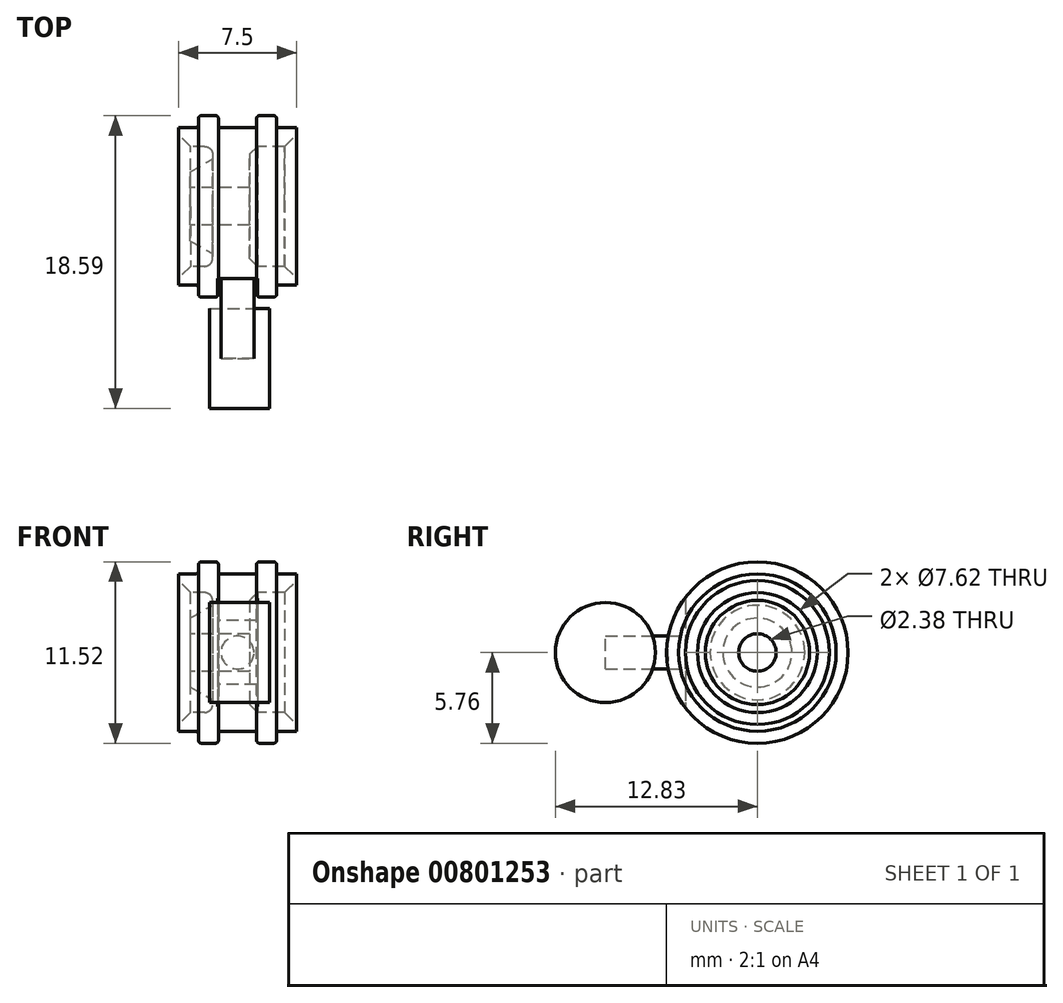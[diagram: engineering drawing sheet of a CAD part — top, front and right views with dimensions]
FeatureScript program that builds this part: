
annotation { "Feature Type Name" : "Feature", "Feature Type Description" : "" }
export const myFeature = defineFeature(function(context is Context, id is Id, definition is map)
    precondition{}
    {
        {
            var Q0;
            Q0=qCreatedBy(makeId("Front.planeOp"),FACE);
            var sketch = newSketch(context, id + "F0", { "sketchPlane" : qUnion([Q0])});
            skLineSegment(sketch, "E0", {"start": v(-3, 1.2) * mm, "end": v(0.76, 1.2) * mm});
            skLineSegment(sketch, "E1", {"start": v(0.76, 1.2) * mm, "end": v(0.76, 3.31) * mm});
            skLineSegment(sketch, "E2", {"start": v(1.26, 3.81) * mm, "end": v(3.75, 3.81) * mm});
            skLineSegment(sketch, "E3", {"start": v(3.75, 3.81) * mm, "end": v(3.75, 5) * mm});
            skLineSegment(sketch, "E4", {"start": v(3.75, 5) * mm, "end": v(2.48, 5) * mm});
            skLineSegment(sketch, "E5", {"start": v(2.48, 5) * mm, "end": v(2.48, 5.76) * mm});
            skLineSegment(sketch, "E6", {"start": v(2.48, 5.76) * mm, "end": v(1.21, 5.76) * mm});
            skLineSegment(sketch, "E7", {"start": v(-2.48, 5.76) * mm, "end": v(-2.48, 5) * mm});
            skLineSegment(sketch, "E8", {"start": v(-2.48, 5) * mm, "end": v(-3.75, 5) * mm});
            skLineSegment(sketch, "E9", {"start": v(-3.75, 5) * mm, "end": v(-3.75, 3.8) * mm});
            skLineSegment(sketch, "E10", {"start": v(-1.59, 3) * mm, "end": v(-3, 2.2) * mm});
            skLineSegment(sketch, "E11", {"start": v(-3, 2.2) * mm, "end": v(-3, 1.2) * mm});
            skLineSegment(sketch, "E12", {"start": v(0, 5.76) * mm, "end": v(0, 0) * mm, "construction": true});
            skLineSegment(sketch, "E13", {"start": v(0, 0) * mm, "end": v(34.63, 0) * mm});
            skLineSegment(sketch, "E14.left", {"start": v(-1.21, 5.76) * mm, "end": v(-1.21, 5) * mm});
            skLineSegment(sketch, "E14.right", {"start": v(1.21, 5.76) * mm, "end": v(1.21, 5) * mm});
            skLineSegment(sketch, "E15.trimOffspring", {"start": v(-1.21, 5.76) * mm, "end": v(-2.48, 5.76) * mm});
            skLineSegment(sketch, "E16", {"start": v(-1.59, 3) * mm, "end": v(-1.59, 3.31) * mm});
            skArc(sketch, "E17.filletArc", {"start": v(-1.59, 3.31) * mm, "mid": v(-1.73, 3.66) * mm, "end": v(-2.09, 3.81) * mm});
            skLineSegment(sketch, "E18", {"start": v(0.76, 3.31) * mm, "end": v(1.26, 3.81) * mm});
            skLineSegment(sketch, "E19", {"start": v(-1.21, 5) * mm, "end": v(1.21, 5) * mm});
            skLineSegment(sketch, "E20", {"start": v(-3.75, 4.4) * mm, "end": v(0, 4.4) * mm, "construction": true});
            skLineSegment(sketch, "E21", {"start": v(0, 4.4) * mm, "end": v(3.75, 4.4) * mm, "construction": true});
            skLineSegment(sketch, "E22", {"start": v(-1.21, 5.76) * mm, "end": v(0, 5.76) * mm, "construction": true});
            skLineSegment(sketch, "E23", {"start": v(0, 5.76) * mm, "end": v(1.21, 5.76) * mm, "construction": true});
            skLineSegment(sketch, "E24", {"start": v(-3.75, 3.81) * mm, "end": v(-2.09, 3.81) * mm});
            skSolve(sketch);
        }
        {
            var Q0;
            Q0=qSketchRegion(id+"F0",true);
            var Q1;
            Q1=sQuery(id+"F0.wireOp",EDGE,"E13");
            revolve(context, id + "F1", {"surfaceOperationType" : NewSurfaceOperationType.NEW, "entities" : qUnion([Q0]), "axis" : qUnion([Q1]), "revolveType" : RevolveType.FULL});
        }
        {
            var Q0;
            Q0=makeQuery(id+"F1.opRevolve","SWEPT_EDGE",EDGE,{"disambiguationData":[OSD([sQuery(id+"F0.wireOp",EDGE,"E5"),sQuery(id+"F0.wireOp",EDGE,"E6")])]});
            var Q1;
            Q1=makeQuery(id+"F1.opRevolve","SWEPT_EDGE",EDGE,{"disambiguationData":[OSD([sQuery(id+"F0.wireOp",EDGE,"E6"),sQuery(id+"F0.wireOp",EDGE,"E7")])]});
            var Q2;
            Q2=makeQuery(id+"F1.opRevolve","SWEPT_EDGE",EDGE,{"disambiguationData":[OSD([sQuery(id+"F0.wireOp",EDGE,"E14.left"),sQuery(id+"F0.wireOp",EDGE,"E15.trimOffspring")])]});
            fillet(context, id + "F2", {"entities" : qUnion([Q0, Q1, Q2]), "radius" : 0.2 * mm, "tangentPropagation" : true, "allowEdgeOverflow" : false});
        }
        {
            var Q0;
            Q0=makeQuery(id+"F1.opRevolve","SWEPT_EDGE",EDGE,{"disambiguationData":[OSD([sQuery(id+"F0.wireOp",EDGE,"E2"),sQuery(id+"F0.wireOp",EDGE,"E3")])]});
            var Q1;
            Q1=makeQuery(id+"F1.opRevolve","SWEPT_EDGE",EDGE,{"disambiguationData":[OSD([sQuery(id+"F0.wireOp",EDGE,"E9"),sQuery(id+"F0.wireOp",EDGE,"E24")])]});
            chamfer(context, id + "F3", {"entities" : qUnion([Q0, Q1]), "width" : 0.76 * mm, "tangentPropagation" : true});
        }
        {
            var Q0;
            Q0=qCreatedBy(makeId("Right.planeOp"),FACE);
            var sketch = newSketch(context, id + "F4", { "sketchPlane" : qUnion([Q0])});
            skLineSegment(sketch, "E25.bottom", {"start": v(-8.57, 4.73) * mm, "end": v(-4.57, 4.73) * mm});
            skLineSegment(sketch, "E25.top", {"start": v(-8.57, -4.76) * mm, "end": v(-4.57, -4.76) * mm});
            skLineSegment(sketch, "E25.left", {"start": v(-8.57, 4.73) * mm, "end": v(-8.57, -4.76) * mm});
            skLineSegment(sketch, "E25.right", {"start": v(-4.57, 4.73) * mm, "end": v(-4.57, -4.76) * mm});
            skSolve(sketch);
        }
        {
            var Q0;
            Q0=qSketchRegion(id+"F4",true);
            extrude(context, id + "F5", {"entities" : qUnion([Q0]), "operationType" : NewBodyOperationType.REMOVE, "oppositeDirection" : true, "depth" : 2.54 * mm, "offsetDistance" : 25.4 * mm, "symmetric" : true});
        }
        {
            var Q0;
            Q0=makeQuery(id+"F5.boolean.opBoolean","COPY",FACE,{"derivedFrom":makeQuery(id+"F5.opExtrude","SWEPT_FACE",FACE,{"disambiguationData":[OSD([sQuery(id+"F4.wireOp",EDGE,"E25.right")])]})});
            var sketch = newSketch(context, id + "F6", { "sketchPlane" : qUnion([Q0])});
            skCircle(sketch, "E26", {"center": v(0, 0) * mm, "radius": 1.05 * mm});
            skSolve(sketch);
        }
        {
            var Q0;
            Q0=qSketchRegion(id+"F6",true);
            extrude(context, id + "F7", {"entities" : qUnion([Q0]), "operationType" : NewBodyOperationType.ADD, "depth" : 5.08 * mm, "offsetDistance" : 25.4 * mm, "hasSecondDirection" : true, "secondDirectionBound" : BoundingType.UP_TO_NEXT, "secondDirectionOppositeDirection" : true, "secondDirectionDepth" : 25.4 * mm});
        }
        {
            var Q0;
            Q0=makeQuery(id+"F7.opExtrude","CAP_FACE",FACE,{"disambiguationData":[OSD([sQuery(id+"F6.wireOp",EDGE,"E26")])],"isStart":false});
            var sketch = newSketch(context, id + "F8", { "sketchPlane" : qUnion([Q0])});
            skLineSegment(sketch, "E27", {"start": v(-1.05, 0) * mm, "end": v(1.05, 0) * mm});
            skSolve(sketch);
        }
        {
            var Q0;
            Q0=makeQuery(id+"F1.opRevolve","SWEPT_FACE",FACE,{"disambiguationData":[OSD([sQuery(id+"F0.wireOp",EDGE,"E1")])]});
            var sketch = newSketch(context, id + "F9", { "sketchPlane" : qUnion([Q0])});
            skCircle(sketch, "E28", {"center": v(-9.65, 0) * mm, "radius": 3.17 * mm});
            skLineSegment(sketch, "E29", {"start": v(-9.65, 0) * mm, "end": v(0, 0) * mm, "construction": true});
            skLineSegment(sketch, "E30", {"start": v(-9.65, 0) * mm, "end": v(-19.3, 0) * mm, "construction": true});
            skSolve(sketch);
        }
        {
            var Q0;
            Q0=qSketchRegion(id+"F9",true);
            extrude(context, id + "F10", {"entities" : qUnion([Q0]), "oppositeDirection" : true, "depth" : 2.54 * mm, "offsetDistance" : 25.4 * mm, "hasSecondDirection" : true, "secondDirectionOppositeDirection" : false, "secondDirectionDepth" : 1.27 * mm});
        }
    });
